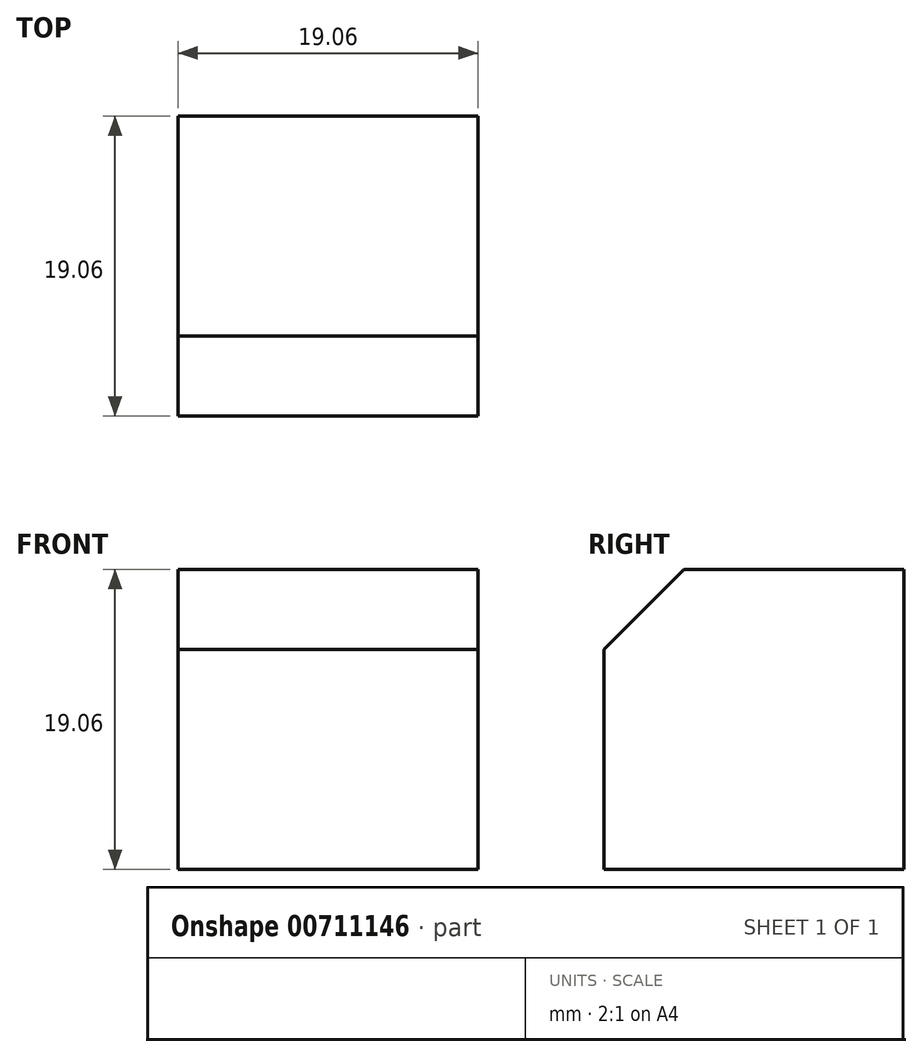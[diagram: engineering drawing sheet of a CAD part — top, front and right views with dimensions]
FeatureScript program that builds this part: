
annotation { "Feature Type Name" : "Feature", "Feature Type Description" : "" }
export const myFeature = defineFeature(function(context is Context, id is Id, definition is map)
    precondition{}
    {
        {
            var Q0;
            Q0=qCreatedBy(makeId("Front.planeOp"),FACE);
            var sketch = newSketch(context, id + "F0", { "sketchPlane" : qUnion([Q0])});
            skLineSegment(sketch, "E0.bottom", {"start": v(-9.52, -9.53) * mm, "end": v(9.52, -9.53) * mm});
            skLineSegment(sketch, "E0.top", {"start": v(-9.53, 9.53) * mm, "end": v(9.52, 9.53) * mm});
            skLineSegment(sketch, "E0.left", {"start": v(-9.52, -9.53) * mm, "end": v(-9.53, 9.53) * mm});
            skLineSegment(sketch, "E0.right", {"start": v(9.52, -9.53) * mm, "end": v(9.52, 9.53) * mm});
            skPoint(sketch, "E0.middle", {"position": v(0, 0) * mm});
            skSolve(sketch);
        }
        {
            var Q0;
            Q0=makeQuery(id+"F0.imprint","IMPRINT",FACE,{"disambiguationData":[TD([[makeQuery(id+"F0.imprint","IMPRINT",EDGE,{"derivedFrom":sQuery(id+"F0.wireOp",EDGE,"E0.bottom")}),1.0]])]});
            extrude(context, id + "F1", {"entities" : qUnion([Q0]), "endBound" : BoundingType.SYMMETRIC, "depth" : 19.05 * mm, "offsetDistance" : 25.4 * mm});
        }
        {
            var Q0;
            Q0=makeQuery(id+"F1.opExtrude","CAP_EDGE",EDGE,{"disambiguationData":[OSD([sQuery(id+"F0.wireOp",EDGE,"E0.top")])],"isStart":false});
            chamfer(context, id + "F2", {"entities" : qUnion([Q0]), "width" : 5.08 * mm, "tangentPropagation" : true});
        }
    });
